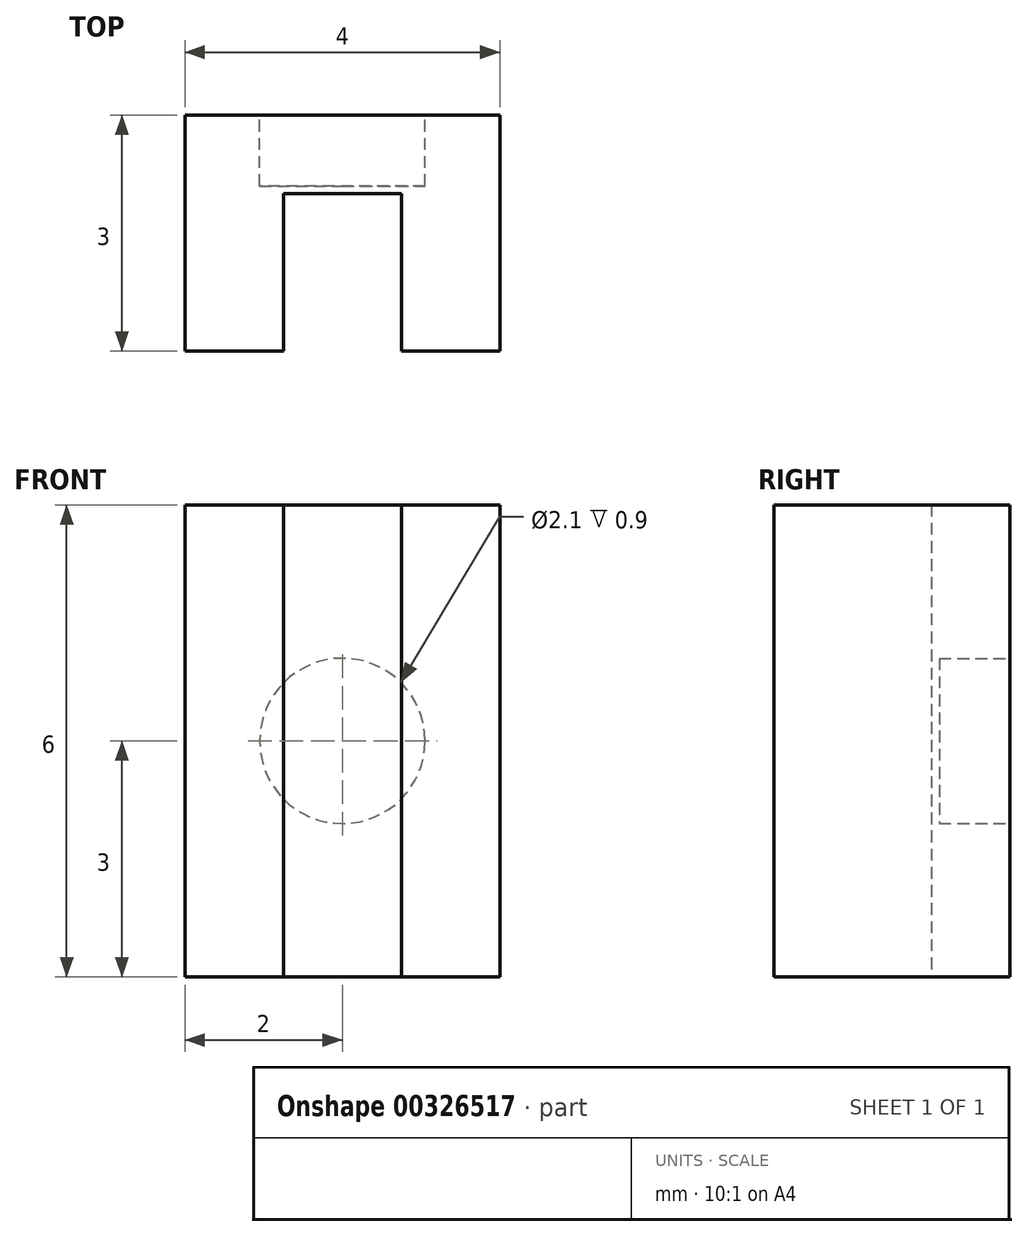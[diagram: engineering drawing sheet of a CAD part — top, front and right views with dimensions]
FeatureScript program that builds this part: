
annotation { "Feature Type Name" : "Feature", "Feature Type Description" : "" }
export const myFeature = defineFeature(function(context is Context, id is Id, definition is map)
    precondition{}
    {
        {
            var Q0;
            Q0=qCreatedBy(makeId("Front.planeOp"),FACE);
            var sketch = newSketch(context, id + "F0", { "sketchPlane" : qUnion([Q0])});
            skLineSegment(sketch, "E0.bottom", {"start": v(-2, 3) * mm, "end": v(2, 3) * mm});
            skLineSegment(sketch, "E0.top", {"start": v(-2, -3) * mm, "end": v(2, -3) * mm});
            skLineSegment(sketch, "E0.left", {"start": v(-2, 3) * mm, "end": v(-2, -3) * mm});
            skLineSegment(sketch, "E0.right", {"start": v(2, 3) * mm, "end": v(2, -3) * mm});
            skPoint(sketch, "E0.middle", {"position": v(0, 0) * mm});
            skSolve(sketch);
        }
        {
            var Q0;
            Q0=makeQuery(id+"F0.imprint","IMPRINT",FACE,{"disambiguationData":[TD([[makeQuery(id+"F0.imprint","IMPRINT",EDGE,{"derivedFrom":sQuery(id+"F0.wireOp",EDGE,"E0.bottom")}),-1.0]])]});
            extrude(context, id + "F1", {"entities" : qUnion([Q0]), "depth" : 3 * mm});
        }
        {
            var Q0;
            Q0=makeQuery(id+"F1.opExtrude","CAP_FACE",FACE,{"disambiguationData":[OSD([sQuery(id+"F0.wireOp",EDGE,"E0.bottom"),sQuery(id+"F0.wireOp",EDGE,"E0.top"),sQuery(id+"F0.wireOp",EDGE,"E0.left"),sQuery(id+"F0.wireOp",EDGE,"E0.right")])],"isStart":false});
            var sketch = newSketch(context, id + "F2", { "sketchPlane" : qUnion([Q0])});
            skLineSegment(sketch, "E1.bottom", {"start": v(-0.75, 3) * mm, "end": v(0.75, 3) * mm});
            skLineSegment(sketch, "E1.top", {"start": v(-0.75, -3) * mm, "end": v(0.75, -3) * mm});
            skLineSegment(sketch, "E1.left", {"start": v(-0.75, 3) * mm, "end": v(-0.75, -3) * mm});
            skLineSegment(sketch, "E1.right", {"start": v(0.75, 3) * mm, "end": v(0.75, -3) * mm});
            skPoint(sketch, "E1.middle", {"position": v(0, 0) * mm});
            skSolve(sketch);
        }
        {
            var Q0;
            Q0=makeQuery(id+"F2.imprint","IMPRINT",FACE,{"disambiguationData":[TD([[makeQuery(id+"F2.imprint","IMPRINT",EDGE,{"derivedFrom":sQuery(id+"F2.wireOp",EDGE,"E1.bottom")}),-1.0]])]});
            extrude(context, id + "F3", {"entities" : qUnion([Q0]), "operationType" : NewBodyOperationType.REMOVE, "oppositeDirection" : true, "depth" : 2 * mm});
        }
        {
            var Q0;
            Q0=makeQuery(id+"F1.opExtrude","CAP_FACE",FACE,{"disambiguationData":[OSD([sQuery(id+"F0.wireOp",EDGE,"E0.bottom"),sQuery(id+"F0.wireOp",EDGE,"E0.top"),sQuery(id+"F0.wireOp",EDGE,"E0.left"),sQuery(id+"F0.wireOp",EDGE,"E0.right")])],"isStart":true});
            var sketch = newSketch(context, id + "F4", { "sketchPlane" : qUnion([Q0])});
            skCircle(sketch, "E2", {"center": v(0, 0) * mm, "radius": 1.05 * mm});
            skSolve(sketch);
        }
        {
            var Q0;
            Q0=makeQuery(id+"F4.imprint","IMPRINT",FACE,{"disambiguationData":[TD([[makeQuery(id+"F4.imprint","IMPRINT",EDGE,{"derivedFrom":sQuery(id+"F4.wireOp",EDGE,"E2")}),1.0]])]});
            extrude(context, id + "F5", {"entities" : qUnion([Q0]), "operationType" : NewBodyOperationType.REMOVE, "oppositeDirection" : true, "depth" : 0.9 * mm});
        }
    });
